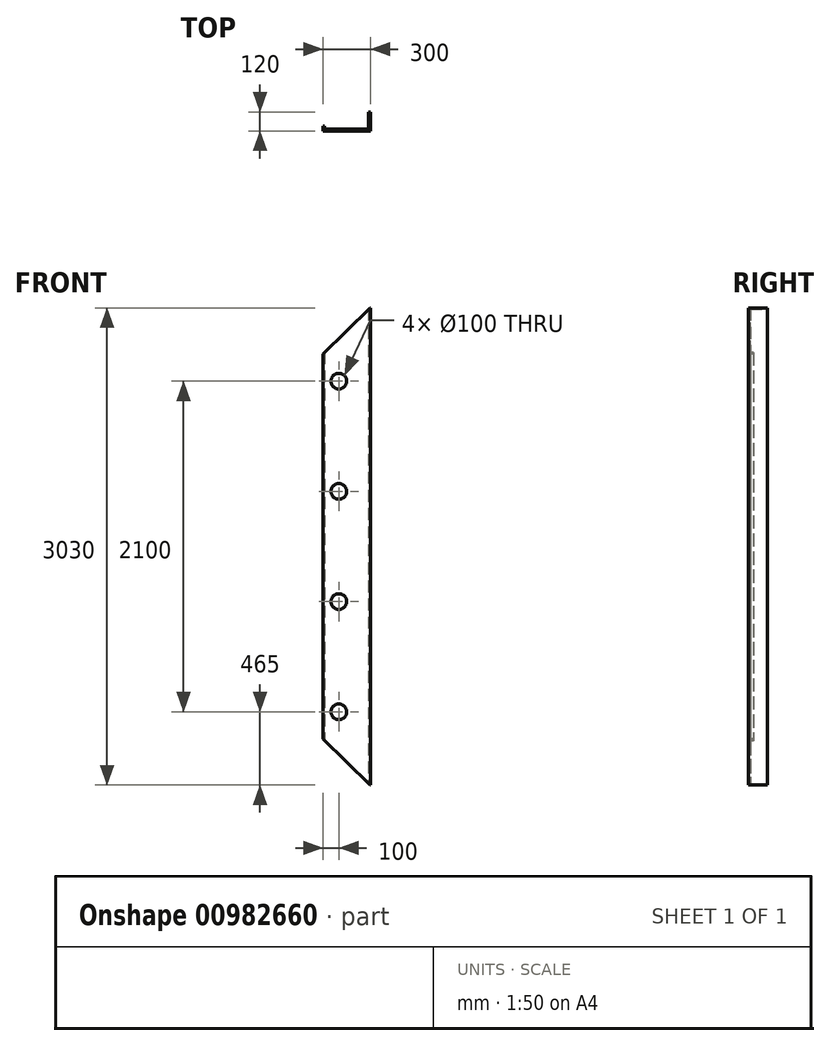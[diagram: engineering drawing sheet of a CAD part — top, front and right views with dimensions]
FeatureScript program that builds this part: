
annotation { "Feature Type Name" : "Feature", "Feature Type Description" : "" }
export const myFeature = defineFeature(function(context is Context, id is Id, definition is map)
    precondition{}
    {
        {
            var Q0;
            Q0=qCreatedBy(makeId("Top.planeOp"),FACE);
            var sketch = newSketch(context, id + "F0", { "sketchPlane" : qUnion([Q0])});
            skLineSegment(sketch, "E0", {"start": v(-110, 0) * mm, "end": v(-100, 0) * mm});
            skLineSegment(sketch, "E1", {"start": v(-100, 0) * mm, "end": v(-100, -20) * mm});
            skLineSegment(sketch, "E2", {"start": v(-100, -20) * mm, "end": v(180, -20) * mm});
            skLineSegment(sketch, "E3", {"start": v(180, -20) * mm, "end": v(180, 90) * mm});
            skLineSegment(sketch, "E4", {"start": v(180, 90) * mm, "end": v(190, 90) * mm});
            skLineSegment(sketch, "E5", {"start": v(190, 90) * mm, "end": v(190, -30) * mm});
            skLineSegment(sketch, "E6", {"start": v(190, -30) * mm, "end": v(-110, -30) * mm});
            skLineSegment(sketch, "E7", {"start": v(-110, -30) * mm, "end": v(-110, 0) * mm});
            skSolve(sketch);
        }
        {
            var Q0;
            Q0=qSketchRegion(id+"F0",true);
            extrude(context, id + "F1", {"entities" : qUnion([Q0]), "depth" : 3030 * mm, "offsetDistance" : 25 * mm});
        }
        {
            var Q0;
            Q0=makeQuery(id+"F1.opExtrude","SWEPT_FACE",FACE,{"disambiguationData":[OSD([sQuery(id+"F0.wireOp",EDGE,"E6")])]});
            var sketch = newSketch(context, id + "F2", { "sketchPlane" : qUnion([Q0])});
            skLineSegment(sketch, "E8", {"start": v(-310, 2542.11) * mm, "end": v(-310, 3230) * mm});
            skLineSegment(sketch, "E9", {"start": v(-310, 3230) * mm, "end": v(390, 3230) * mm});
            skLineSegment(sketch, "E10", {"start": v(390, 3230) * mm, "end": v(-310, 2542.11) * mm});
            skLineSegment(sketch, "E11", {"start": v(-2423.37, 1515) * mm, "end": v(3096.96, 1515) * mm});
            skLineSegment(sketch, "E12.MirrorCS", {"start": v(-310, -200) * mm, "end": v(390, -200) * mm});
            skLineSegment(sketch, "E13.MirrorCS", {"start": v(-310, 487.89) * mm, "end": v(-310, -200) * mm});
            skLineSegment(sketch, "E14.MirrorCS", {"start": v(390, -200) * mm, "end": v(-310, 487.89) * mm});
            skSolve(sketch);
        }
        {
            var Q0;
            {var subQ0=sQuery(id+"F2.wireOp",EDGE,"E14.MirrorCS");var subQ1=sQuery(id+"F0.wireOp",EDGE,"E6");var subQ2=makeQuery(id+"F1.opExtrude","CAP_EDGE",EDGE,{"disambiguationData":[OSD([subQ1])],"isStart":true});var subQ3=makeQuery(id+"F2.imprint","INTERSECT",VERTEX,{"derivedFrom":[subQ2,subQ0]});Q0=makeQuery(id+"F2.imprint","IMPRINT",FACE,{"disambiguationData":[TD([[makeQuery(id+"F2.imprint","IMPRINT",EDGE,{"disambiguationData":[TD([[subQ3,-1.0]])],"derivedFrom":subQ0}),1.0]])]});}
            var Q1;
            {var subQ0=sQuery(id+"F2.wireOp",EDGE,"E10");var subQ1=sQuery(id+"F0.wireOp",EDGE,"E6");var subQ2=makeQuery(id+"F1.opExtrude","CAP_EDGE",EDGE,{"disambiguationData":[OSD([subQ1])],"isStart":false});var subQ3=makeQuery(id+"F2.imprint","INTERSECT",VERTEX,{"derivedFrom":[subQ2,subQ0]});Q1=makeQuery(id+"F2.imprint","IMPRINT",FACE,{"disambiguationData":[TD([[makeQuery(id+"F2.imprint","IMPRINT",EDGE,{"disambiguationData":[TD([[subQ3,-1.0]])],"derivedFrom":subQ0}),-1.0]])]});}
            extrude(context, id + "F3", {"entities" : qUnion([Q0, Q1]), "operationType" : NewBodyOperationType.REMOVE, "oppositeDirection" : true, "depth" : 200 * mm, "offsetDistance" : 25 * mm});
        }
        {
            var Q0;
            Q0=makeQuery(id+"F1.opExtrude","SWEPT_FACE",FACE,{"disambiguationData":[OSD([sQuery(id+"F0.wireOp",EDGE,"E6")])]});
            var sketch = newSketch(context, id + "F4", { "sketchPlane" : qUnion([Q0])});
            skCircle(sketch, "E15", {"center": v(-10, 2565) * mm, "radius": 50 * mm});
            skCircle(sketch, "E16.0.1.0", {"center": v(-10, 1865) * mm, "radius": 50 * mm});
            skCircle(sketch, "E16.0.2.0", {"center": v(-10, 1165) * mm, "radius": 50 * mm});
            skLineSegment(sketch, "E16.direction1", {"start": v(15, 1580) * mm, "end": v(894.74, 1580) * mm, "construction": true});
            skLineSegment(sketch, "E16.direction2", {"start": v(894.74, 1580) * mm, "end": v(894.74, 780) * mm, "construction": true});
            skCircle(sketch, "E17.0.0.3", {"center": v(-10, 465) * mm, "radius": 50 * mm});
            skSolve(sketch);
        }
        {
            var Q0;
            Q0=makeQuery(id+"F4.imprint","IMPRINT",FACE,{"disambiguationData":[TD([[makeQuery(id+"F4.imprint","IMPRINT",EDGE,{"derivedFrom":sQuery(id+"F4.wireOp",EDGE,"E17.0.0.3")}),1.0]])]});
            var Q1;
            Q1=makeQuery(id+"F4.imprint","IMPRINT",FACE,{"disambiguationData":[TD([[makeQuery(id+"F4.imprint","IMPRINT",EDGE,{"derivedFrom":sQuery(id+"F4.wireOp",EDGE,"E16.0.2.0")}),1.0]])]});
            var Q2;
            Q2=makeQuery(id+"F4.imprint","IMPRINT",FACE,{"disambiguationData":[TD([[makeQuery(id+"F4.imprint","IMPRINT",EDGE,{"derivedFrom":sQuery(id+"F4.wireOp",EDGE,"E16.0.1.0")}),1.0]])]});
            var Q3;
            Q3=makeQuery(id+"F4.imprint","IMPRINT",FACE,{"disambiguationData":[TD([[makeQuery(id+"F4.imprint","IMPRINT",EDGE,{"derivedFrom":sQuery(id+"F4.wireOp",EDGE,"E15")}),1.0]])]});
            extrude(context, id + "F5", {"entities" : qUnion([Q0, Q1, Q2, Q3]), "operationType" : NewBodyOperationType.REMOVE, "endBound" : BoundingType.THROUGH_ALL, "oppositeDirection" : true, "depth" : 25 * mm, "offsetDistance" : 25 * mm});
        }
    });
